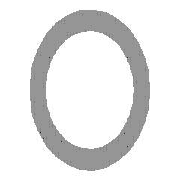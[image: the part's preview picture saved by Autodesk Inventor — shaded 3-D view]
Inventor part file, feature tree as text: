
AUTODESK INVENTOR PART (.ipt)
format: ipt  version: 2021 (Build 250183000, 183)  size: 302,592 bytes
history: native  units: mm (DEFAULTED — no unit token found)
features: other x11, plane x2, sketch x2, sweep x1
ambient origin geometry x8: Origin, YZ Plane, XZ Plane, XY Plane, X Axis, Y Axis, Z Axis, Center Point
bodies: Solid1 (feature_tree)
feature tree (16):
  parser-record x1  (decoder bookkeeping rows leaked as tree rows — omitted from the tree; the rows remain in map.json)
  other  "Driven Length"
  other  "Plano inicial"
  other  "Plano final"
  other  "Trayectoria de barrido"
  plane  "Plano de trabajo de orientación"
  sweep  "Cuerpo"
  sketch  "Sketch3"  dims[d0=26.67mm d1=2.8702mm]
  plane  "Work Plane3"
  sketch  "Sketch4"  dims[d4=-0.0mm d5=545.971932mm d6=90.0deg d7=545.971932mm d8=0.0mm d9=0.0mm d182=5.0mm d183=0.0mm d184=5.0mm d185=0.0mm]
  other  "Sup121"
  other  "Sup122"
  other  "Sólido40"
  other  "Sup120"
  other  "Superficie de contorno77"
  other  "Superficie de contorno78"
